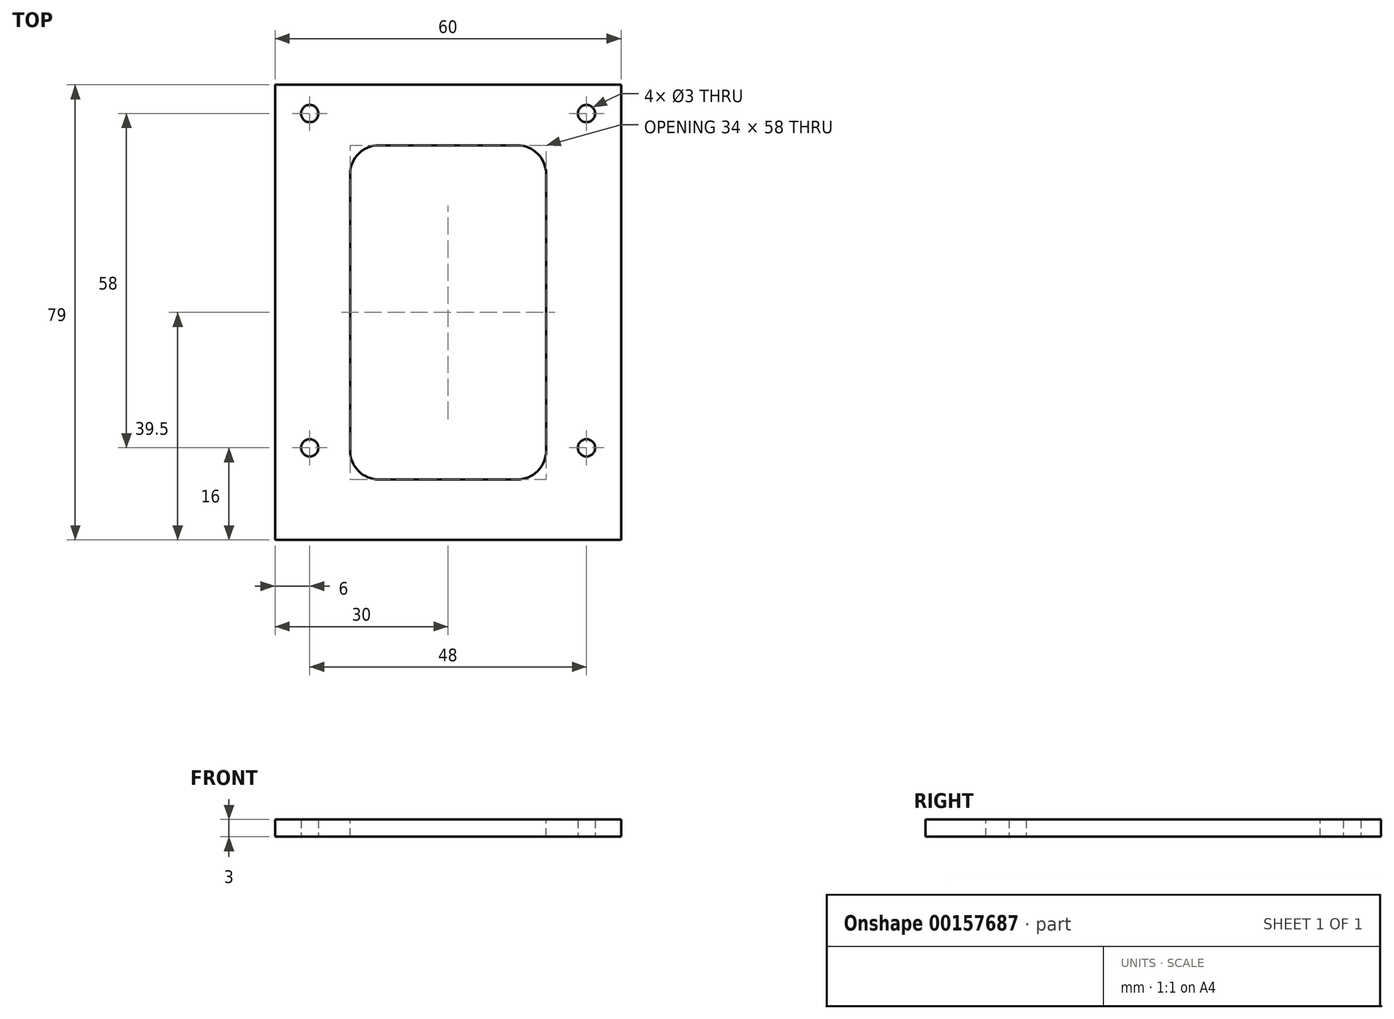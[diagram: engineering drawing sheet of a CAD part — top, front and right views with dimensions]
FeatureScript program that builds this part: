
annotation { "Feature Type Name" : "Feature", "Feature Type Description" : "" }
export const myFeature = defineFeature(function(context is Context, id is Id, definition is map)
    precondition{}
    {
        {
            var Q0;
            Q0=qCreatedBy(makeId("Top.planeOp"),FACE);
            var sketch = newSketch(context, id + "F0", { "sketchPlane" : qUnion([Q0])});
            skLineSegment(sketch, "E0.bottom", {"start": v(30, 39.5) * mm, "end": v(-30, 39.5) * mm});
            skLineSegment(sketch, "E0.top", {"start": v(30, -39.5) * mm, "end": v(-30, -39.5) * mm});
            skLineSegment(sketch, "E0.left", {"start": v(30, 39.5) * mm, "end": v(30, -39.5) * mm});
            skLineSegment(sketch, "E0.right", {"start": v(-30, 39.5) * mm, "end": v(-30, -39.5) * mm});
            skPoint(sketch, "E0.middle", {"position": v(0, 0) * mm});
            skCircle(sketch, "E1", {"center": v(-24, 34.5) * mm, "radius": 1.5 * mm});
            skCircle(sketch, "E2.MirrorC", {"center": v(24, 34.5) * mm, "radius": 1.5 * mm});
            skCircle(sketch, "E3", {"center": v(-24, -23.5) * mm, "radius": 1.5 * mm});
            skCircle(sketch, "E4.MirrorC", {"center": v(24, -23.5) * mm, "radius": 1.5 * mm});
            skSolve(sketch);
        }
        {
            var Q0;
            Q0 = qSketchRegion(id + "F0", true);
            extrude(context, id + "F1", {"entities" : qUnion([Q0]), "depth" : 3 * mm});
        }
        {
            var Q0;
            Q0=makeQuery(id+"F1.opExtrude","CAP_FACE",FACE,{"disambiguationData":[OSD([sQuery(id+"F0.wireOp",EDGE,"E0.bottom"),sQuery(id+"F0.wireOp",EDGE,"E0.top"),sQuery(id+"F0.wireOp",EDGE,"E0.left"),sQuery(id+"F0.wireOp",EDGE,"E0.right"),sQuery(id+"F0.wireOp",EDGE,"E1"),sQuery(id+"F0.wireOp",EDGE,"E2.MirrorC"),sQuery(id+"F0.wireOp",EDGE,"E3"),sQuery(id+"F0.wireOp",EDGE,"E4.MirrorC")])],"isStart":false});
            var sketch = newSketch(context, id + "F2", { "sketchPlane" : qUnion([Q0])});
            skLineSegment(sketch, "E5.bottom", {"start": v(-17, 29) * mm, "end": v(17, 29) * mm});
            skLineSegment(sketch, "E5.top", {"start": v(-17, -29) * mm, "end": v(17, -29) * mm});
            skLineSegment(sketch, "E5.left", {"start": v(-17, 29) * mm, "end": v(-17, -29) * mm});
            skLineSegment(sketch, "E5.right", {"start": v(17, 29) * mm, "end": v(17, -29) * mm});
            skPoint(sketch, "E5.middle", {"position": v(0, 0) * mm});
            skSolve(sketch);
        }
        {
            var Q0;
            Q0 = qSketchRegion(id + "F2", true);
            extrude(context, id + "F3", {"entities" : qUnion([Q0]), "operationType" : NewBodyOperationType.REMOVE, "endBound" : BoundingType.UP_TO_NEXT, "oppositeDirection" : true, "depth" : 25 * mm});
        }
        {
            var Q0;
            Q0=makeQuery(id+"F3.boolean.opBoolean","COPY",EDGE,{"derivedFrom":makeQuery(id+"F3.opExtrude","SWEPT_EDGE",EDGE,{"disambiguationData":[OSD([sQuery(id+"F2.wireOp",EDGE,"E5.bottom"),sQuery(id+"F2.wireOp",EDGE,"E5.left")])]})});
            fillet(context, id + "F4", {"entities" : qUnion([Q0]), "radius" : 5 * mm, "tangentPropagation" : true, "allowEdgeOverflow" : false});
        }
        {
            var Q0;
            Q0=makeQuery(id+"F3.boolean.opBoolean","COPY",EDGE,{"derivedFrom":makeQuery(id+"F3.opExtrude","SWEPT_EDGE",EDGE,{"disambiguationData":[OSD([sQuery(id+"F2.wireOp",EDGE,"E5.top"),sQuery(id+"F2.wireOp",EDGE,"E5.left")])]})});
            var Q1;
            Q1=makeQuery(id+"F3.boolean.opBoolean","COPY",EDGE,{"derivedFrom":makeQuery(id+"F3.opExtrude","SWEPT_EDGE",EDGE,{"disambiguationData":[OSD([sQuery(id+"F2.wireOp",EDGE,"E5.top"),sQuery(id+"F2.wireOp",EDGE,"E5.right")])]})});
            var Q2;
            Q2=makeQuery(id+"F3.boolean.opBoolean","COPY",EDGE,{"derivedFrom":makeQuery(id+"F3.opExtrude","SWEPT_EDGE",EDGE,{"disambiguationData":[OSD([sQuery(id+"F2.wireOp",EDGE,"E5.bottom"),sQuery(id+"F2.wireOp",EDGE,"E5.right")])]})});
            fillet(context, id + "F5", {"entities" : qUnion([Q0, Q1, Q2]), "radius" : 5 * mm, "tangentPropagation" : true, "allowEdgeOverflow" : false});
        }
    });
